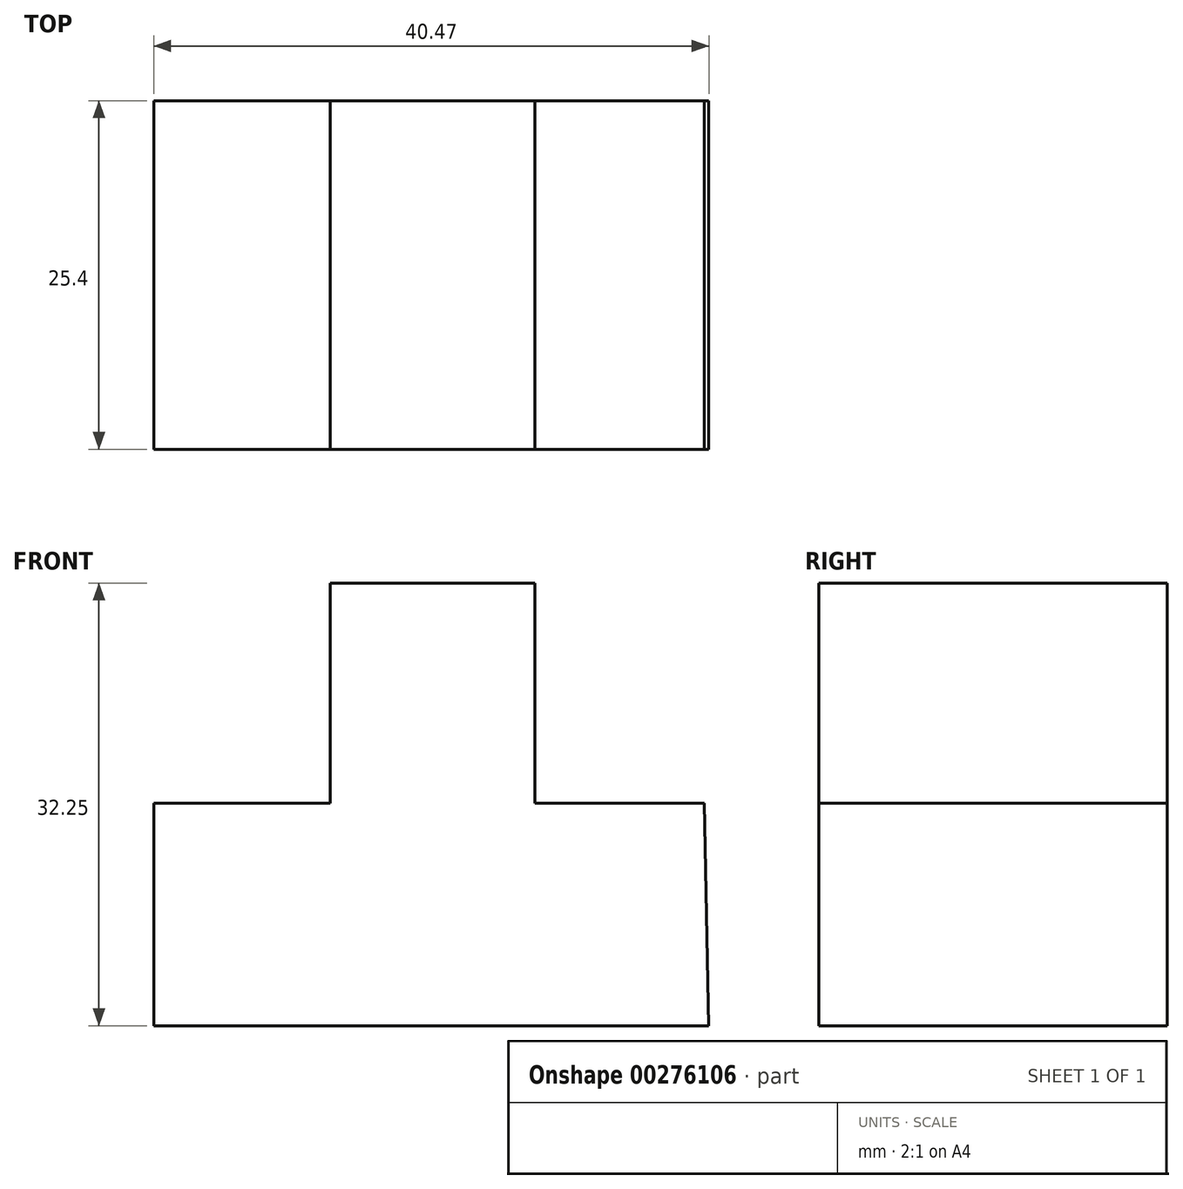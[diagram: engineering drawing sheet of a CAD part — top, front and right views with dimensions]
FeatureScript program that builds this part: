
annotation { "Feature Type Name" : "Feature", "Feature Type Description" : "" }
export const myFeature = defineFeature(function(context is Context, id is Id, definition is map)
    precondition{}
    {
        {
            var Q0;
            Q0=qCreatedBy(makeId("Front.planeOp"),FACE);
            var sketch = newSketch(context, id + "F0", { "sketchPlane" : qUnion([Q0])});
            skLineSegment(sketch, "E0", {"start": v(-14.93, 0) * mm, "end": v(-55.4, 0) * mm});
            skLineSegment(sketch, "E1", {"start": v(-55.4, 16.2) * mm, "end": v(-42.55, 16.2) * mm});
            skLineSegment(sketch, "E2", {"start": v(-42.55, 16.2) * mm, "end": v(-42.55, 32.25) * mm});
            skLineSegment(sketch, "E3", {"start": v(-42.55, 32.25) * mm, "end": v(-27.62, 32.25) * mm});
            skLineSegment(sketch, "E4", {"start": v(-27.62, 32.25) * mm, "end": v(-27.62, 16.2) * mm});
            skLineSegment(sketch, "E5", {"start": v(-27.62, 16.2) * mm, "end": v(-15.25, 16.2) * mm});
            skLineSegment(sketch, "E6", {"start": v(-15.25, 16.2) * mm, "end": v(-14.93, 0) * mm});
            skLineSegment(sketch, "E7", {"start": v(-55.4, 16.2) * mm, "end": v(-55.4, 0) * mm});
            skSolve(sketch);
        }
        {
            var Q0;
            Q0=makeQuery(id+"F0.imprint","IMPRINT",FACE,{"disambiguationData":[TD([[makeQuery(id+"F0.imprint","IMPRINT",EDGE,{"derivedFrom":sQuery(id+"F0.wireOp",EDGE,"E0")}),-1.0]])]});
            extrude(context, id + "F1", {"entities" : qUnion([Q0]), "depth" : 25.4 * mm});
        }
    });
